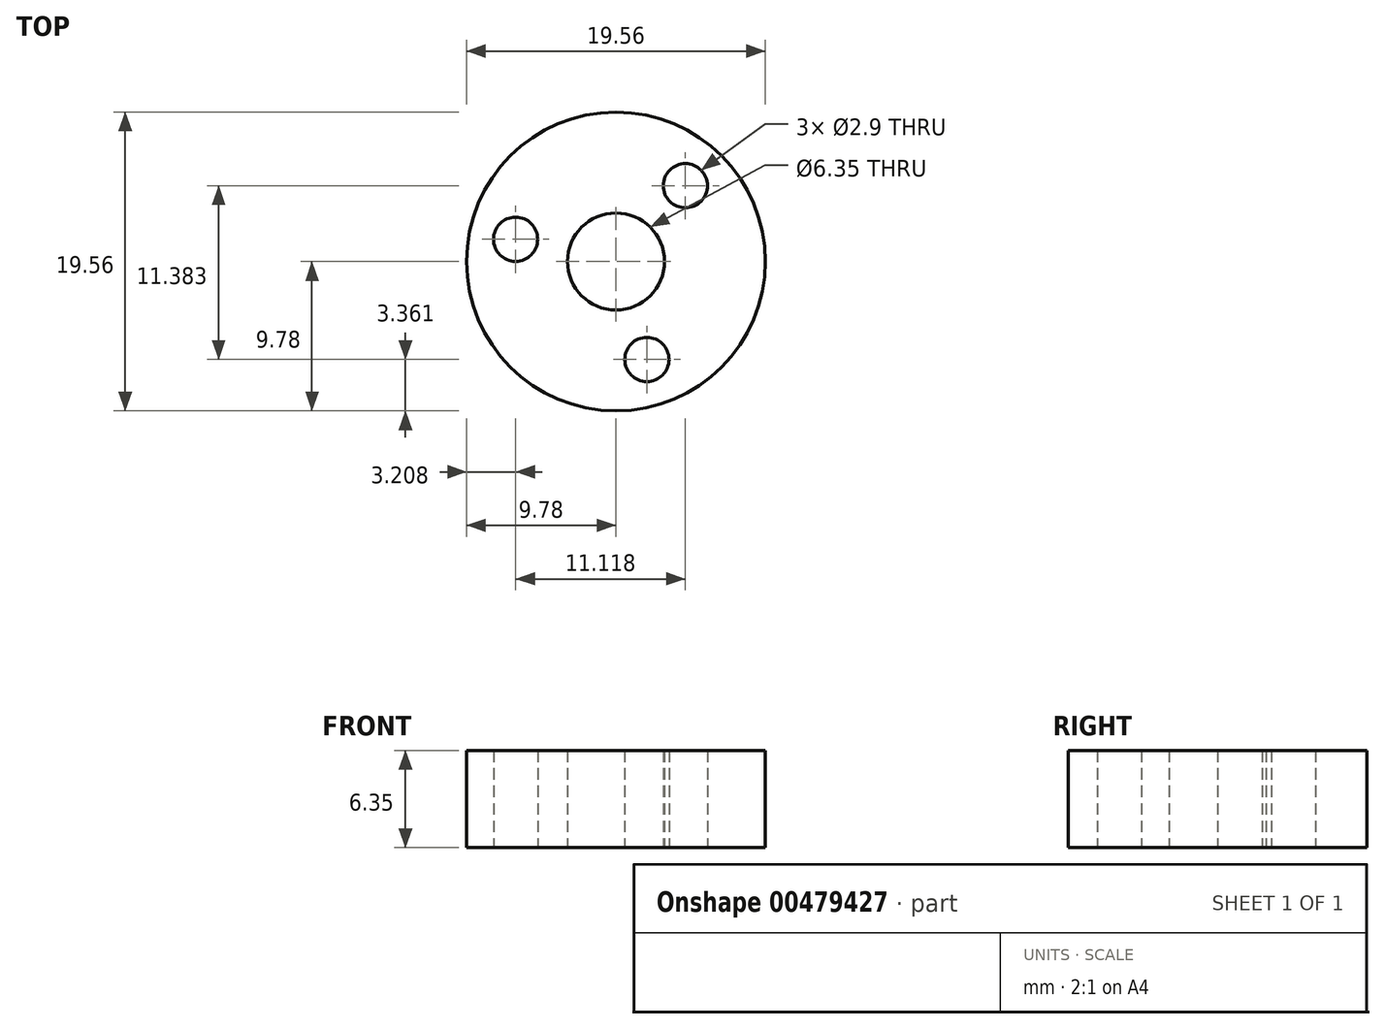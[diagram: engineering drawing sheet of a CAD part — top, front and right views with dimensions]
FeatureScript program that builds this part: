
annotation { "Feature Type Name" : "Feature", "Feature Type Description" : "" }
export const myFeature = defineFeature(function(context is Context, id is Id, definition is map)
    precondition{}
    {
        {
            var Q0;
            Q0=qCreatedBy(makeId("Top.planeOp"),FACE);
            var sketch = newSketch(context, id + "F0", { "sketchPlane" : qUnion([Q0])});
            skCircle(sketch, "E0", {"center": v(0, 0) * mm, "radius": 9.78 * mm});
            skCircle(sketch, "E1", {"center": v(0, 0) * mm, "radius": 3.18 * mm});
            skLineSegment(sketch, "E2", {"start": v(0, 0) * mm, "end": v(2.03, -6.42) * mm});
            skLineSegment(sketch, "E3", {"start": v(4.55, 4.96) * mm, "end": v(0, 0) * mm});
            skLineSegment(sketch, "E4", {"start": v(0, 0) * mm, "end": v(-6.57, 1.46) * mm});
            skCircle(sketch, "E5", {"center": v(-6.57, 1.46) * mm, "radius": 1.45 * mm});
            skCircle(sketch, "E6", {"center": v(4.55, 4.96) * mm, "radius": 1.45 * mm});
            skCircle(sketch, "E7", {"center": v(2.03, -6.42) * mm, "radius": 1.45 * mm});
            skSolve(sketch);
        }
        {
            var Q0;
            Q0=makeQuery(id+"F0.imprint","IMPRINT",FACE,{"disambiguationData":[TD([[makeQuery(id+"F0.imprint","IMPRINT",EDGE,{"derivedFrom":sQuery(id+"F0.wireOp",EDGE,"E0")}),1.0]])]});
            var Q1;
            {var subQ5=sQuery(id+"F0.wireOp",EDGE,"E4");var subQ6=sQuery(id+"F0.wireOp",EDGE,"E1");var subQ7=makeQuery(id+"F0.imprint","INTERSECT",VERTEX,{"derivedFrom":[subQ6,subQ5]});Q1=makeQuery(id+"F0.imprint","IMPRINT",FACE,{"disambiguationData":[TD([[makeQuery(id+"F0.imprint","IMPRINT",EDGE,{"disambiguationData":[TD([[subQ7,1.0]])],"derivedFrom":subQ6}),-1.0]])]});}
            var Q2;
            {var subQ0=sQuery(id+"F0.wireOp",EDGE,"E3");var subQ1=sQuery(id+"F0.wireOp",EDGE,"E1");var subQ2=makeQuery(id+"F0.imprint","INTERSECT",VERTEX,{"derivedFrom":[subQ1,subQ0]});Q2=makeQuery(id+"F0.imprint","IMPRINT",FACE,{"disambiguationData":[TD([[makeQuery(id+"F0.imprint","IMPRINT",EDGE,{"disambiguationData":[TD([[subQ2,1.0]])],"derivedFrom":subQ1}),-1.0]])]});}
            var Q3;
            {var subQ0=sQuery(id+"F0.wireOp",EDGE,"E4");var subQ1=sQuery(id+"F0.wireOp",EDGE,"E1");var subQ2=makeQuery(id+"F0.imprint","INTERSECT",VERTEX,{"derivedFrom":[subQ1,subQ0]});Q3=makeQuery(id+"F0.imprint","IMPRINT",FACE,{"disambiguationData":[TD([[makeQuery(id+"F0.imprint","IMPRINT",EDGE,{"disambiguationData":[TD([[subQ2,-1.0]])],"derivedFrom":subQ1}),-1.0]])]});}
            extrude(context, id + "F1", {"entities" : qUnion([Q0, Q1, Q2, Q3]), "depth" : 6.35 * mm, "offsetDistance" : 25.4 * mm});
        }
    });
